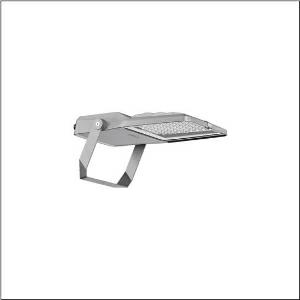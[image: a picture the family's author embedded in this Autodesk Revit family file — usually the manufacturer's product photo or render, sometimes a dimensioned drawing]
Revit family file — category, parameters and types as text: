
# Revit family: floodlight_fl_21_iq_mini___pl43_5xa7772c4a1a_8d49
name_source: partatom
category: Lighting Fixtures
units: mm (PartAtom-declared; Revit-internal decimal feet)

## family parameters
Cut with Voids When Loaded = No
Host = Face
Light Source = No
Part Type = Normal
Room Calculation Point = No
Round Connector Dimension = Use Diameter
Shared = No

## types (1)
- --- (1 x LED, 13050 lm, 87.2 W, 4000K)
    Apparent Load = 87 VA
    CIE Flux Codes = 27 78 99 100 100
    Color Rendering = 70
    Color Temperature = 4000K
    Default Elevation = 1800 mm
    Description = Floodlight FL 21 iQ mini, floodlight, primary light control with lens, of PMMA, primary optical cover: protective disc, of toughened safety glass, transparent, light distribution: PL43, light emission: direct distribution, installation type: surface-mounted, LED, High Power LED, rated luminous flux: 13.050lm, luminous efficacy: 150lm/W, light colour: 740, colour temperature: 4000K, control gear: iQ Street-Remote/DALI, control: Street-Remote, Auto-Match, Temp-Guard, Night-Set, Smart-Wire, Desk-Remote (wireless, voltage-free reading and setting of iQ features in the workshop via application-optimized NFC function/RFID function), optimised constant luminous flux control (CLO 2.0), with terminal, 6-pole, mains connection: 220..240V, AC, 50/60Hz, start of lifetime: 87W, end of service life: 92W, reduction: 40W, luminaire housing, of diecast aluminium, powder-coated, Siteco® metallic grey (DB 702S), corrosivity category C5 mid according to DIN EN ISO 12944, suitable for swimming pools, chlorine-resistant, sealing non-destructively replaceable, mounting bracket, of steel, galvanised, powder-coated, Siteco® metallic grey (DB 702S), protection rating (complete): IP66, insulation class (complete): insulation class II (safety insulation), certification: CE, ENEC, VDE, protection symbol: D, impact resistance: IK08, permissible operating ambient temperature: -40..+40°C, permissible operating ambient temperature for outdoor applications: -40..+50°C, standard: DIN EN 12944, LABS conformity tested according to VDMA 24364:2018-05, packaging unit: 1 piece

Light Distribution: PL43
    Height = 70 mm
    Lamp = 1 x LED
    Lamp Light Flux = 13050 lm
    Lamp Power = 87.2 W
    Lamp count = 1
    Length = 485 mm
    Luminous efficacy = 150 lm/W
    Manufacturer = Siteco
    ModVariant = No
    Model = 5XA7772C4A1A
    Number of Poles = 1
    OnlyDefault = Yes
    Power Factor = 1
    Product Name = Floodlight FL 21 iQ mini | PL43
    Product group = floodlight | pylon annexe
    ProductGroupID = 6200
    Protection Class = Protection class II
    Protection Degree = IP 66
    RLX_Detail_Level = 1
    RLX_Emergency_Light_Flux = 0 lm
    RLX_Emergency_Type = 0
    RLX_Emergency_Type_DB = No
    RlxData = <blob elided: 96309 chars, md5=bfd7cc71>
    Socket = socket
    Standby Power = 0 W
    System Light Flux = 13050 lm
    System Power = 87 W
    Type Comments = factory setting: luminous flux: 100 % | dim-lin: 254 | 456 mA
    Type Image = l_1006845.jpg
    URL = http://relux.com
    VarID = @adj_161830
    Voltage = 0 V
    Weight = 0.00 kg
    Width = 337 mm

## geometry (parser evidence)
native form markers: Blend x4, Sweep x11
no freeform markers — native parametric forms only
